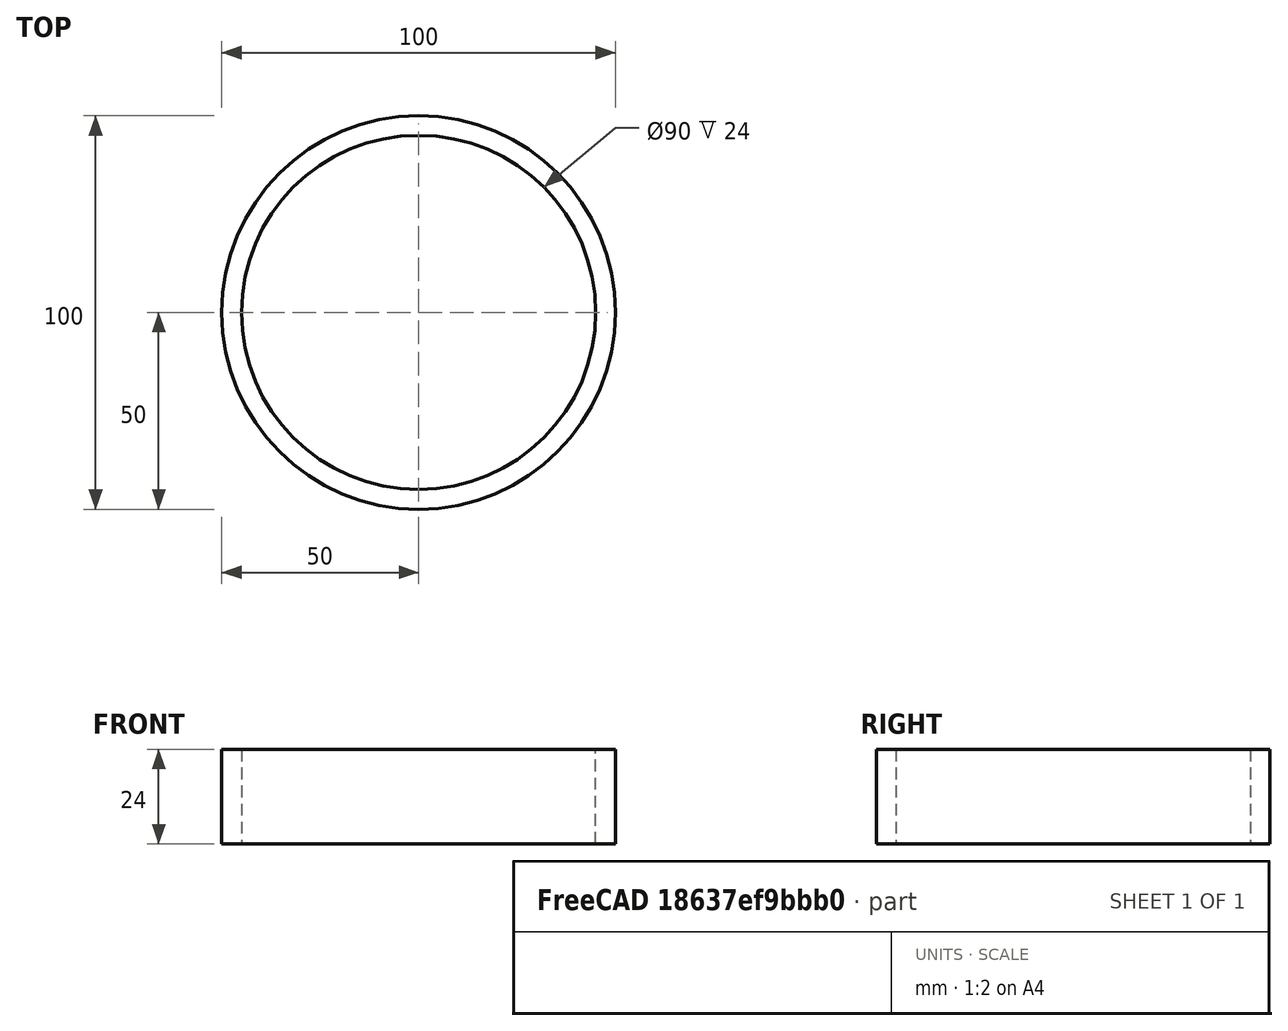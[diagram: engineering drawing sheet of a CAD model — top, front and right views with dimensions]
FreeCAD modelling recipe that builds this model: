
FCSTD DOCUMENT  (FreeCAD 0.19R24276 (Git))
Label: Ring_90x100x24_IN
License: All rights reserved
LicenseURL: http://en.wikipedia.org/wiki/All_rights_reserved
objects: Sketcher::SketchObject×1, PartDesign::Pad×1, PartDesign::Body×1
note: 4 computed .brp shape members not serialized (recipe doc carries the construction recipe); baked Part::Feature solids carry a one-line shape summary decoded from their .brp

FEATURE [Sketcher::SketchObject] Sketch
  FullyConstrained = true
  MapMode = 5
  Support = -> [XY_Plane]
  sketch-geometry (2):
    g0: Circle CenterX=0 CenterY=0 CenterZ=0 NormalX=0 NormalY=0 NormalZ=1 AngleXU=0 Radius=50
    g1: Circle CenterX=0 CenterY=0 CenterZ=0 NormalX=0 NormalY=0 NormalZ=1 AngleXU=0 Radius=45
  constraints (4):
    c: Coincident(g1,g0)
    c: Diameter(g1) = 90
    c: Diameter(g0) = 100
    c: Coincident(g0,g-1)
FEATURE [PartDesign::Pad] Pad
  Direction = (1,1,1)
  Length = 24
  Length2 = 100
  Profile = -> Sketch
  Type = 0
FEATURE [PartDesign::Body] Body  label="Body_ring_in"
  Group = -> [Sketch,Pad]
  Origin = -> Origin
  Tip = -> Pad
